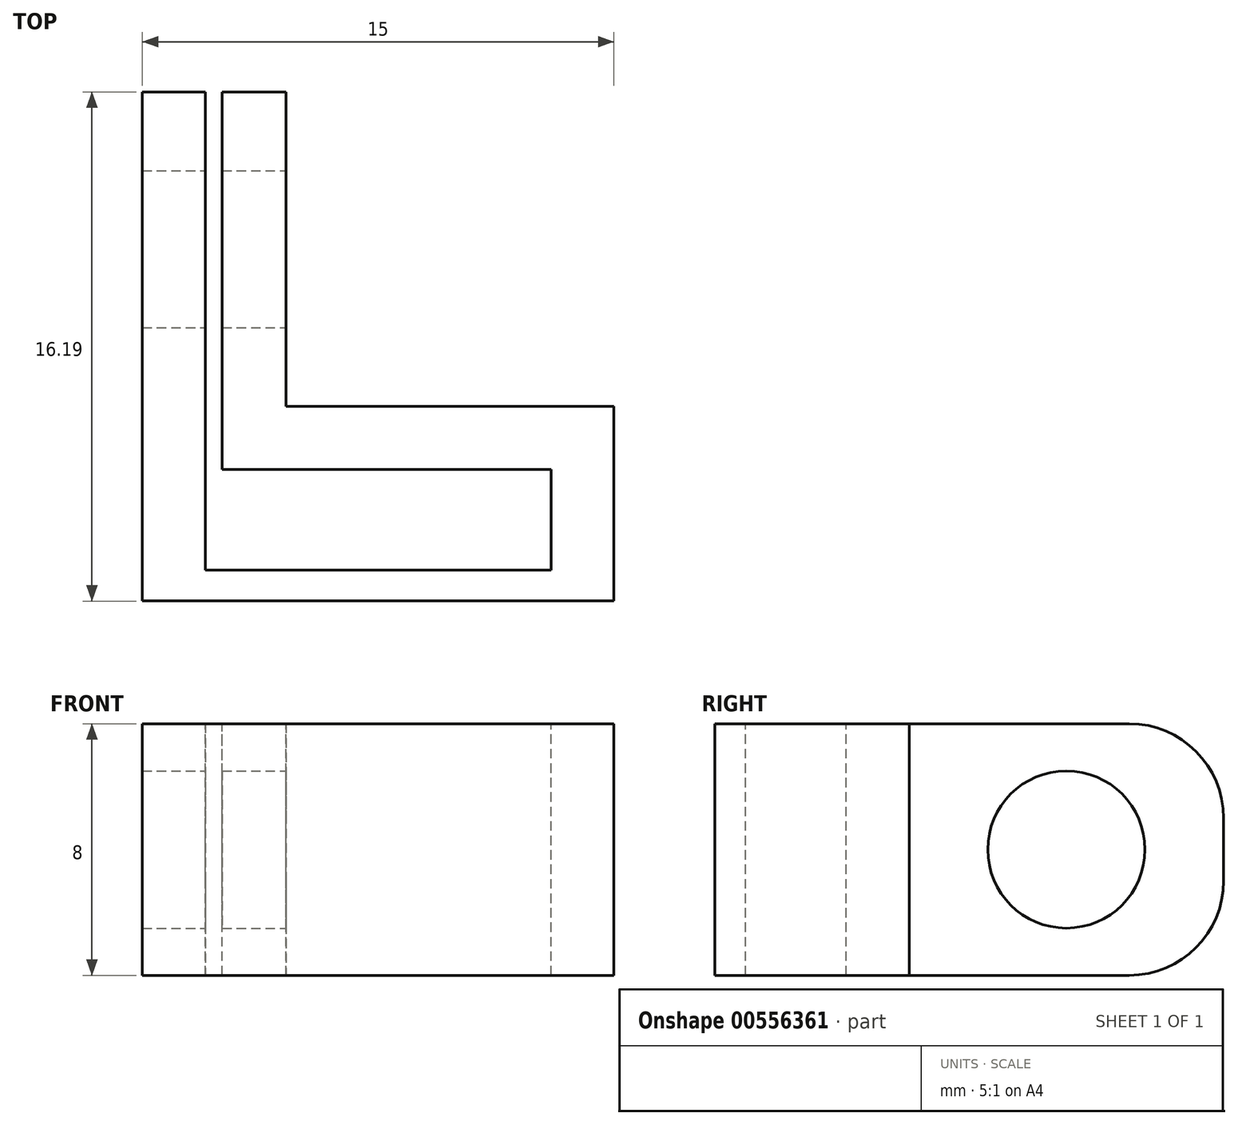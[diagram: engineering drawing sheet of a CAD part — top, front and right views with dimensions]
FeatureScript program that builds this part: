
annotation { "Feature Type Name" : "Feature", "Feature Type Description" : "" }
export const myFeature = defineFeature(function(context is Context, id is Id, definition is map)
    precondition{}
    {
        {
            var Q0;
            Q0=qCreatedBy(makeId("Top.planeOp"),FACE);
            var sketch = newSketch(context, id + "F0", { "sketchPlane" : qUnion([Q0])});
            skLineSegment(sketch, "E0", {"start": v(0, 15.2) * mm, "end": v(0, 0) * mm});
            skLineSegment(sketch, "E1", {"start": v(0, 0) * mm, "end": v(11, 0) * mm});
            skLineSegment(sketch, "E2", {"start": v(11, 0) * mm, "end": v(11, 3.2) * mm});
            skLineSegment(sketch, "E3", {"start": v(11, 3.2) * mm, "end": v(0.54, 3.2) * mm});
            skLineSegment(sketch, "E4", {"start": v(0.54, 3.2) * mm, "end": v(0.54, 15.2) * mm});
            skLineSegment(sketch, "E5", {"start": v(0.54, 15.2) * mm, "end": v(0.57, 15.2) * mm});
            skLineSegment(sketch, "E6", {"start": v(2.57, 5.2) * mm, "end": v(13, 5.2) * mm});
            skLineSegment(sketch, "E7", {"start": v(13, 5.2) * mm, "end": v(13, -0.99) * mm});
            skLineSegment(sketch, "E8", {"start": v(13, -0.99) * mm, "end": v(-2, -0.99) * mm});
            skLineSegment(sketch, "E9", {"start": v(-2, -0.99) * mm, "end": v(-2, 15.2) * mm});
            skLineSegment(sketch, "E10", {"start": v(-2, 15.2) * mm, "end": v(0, 15.2) * mm});
            skLineSegment(sketch, "E11", {"start": v(0.57, 15.2) * mm, "end": v(2.57, 15.2) * mm});
            skLineSegment(sketch, "E12", {"start": v(2.57, 15.2) * mm, "end": v(2.57, 5.2) * mm});
            skSolve(sketch);
        }
        {
            var Q0;
            Q0 = qSketchRegion(id + "F0", true);
            extrude(context, id + "F1", {"entities" : qUnion([Q0]), "oppositeDirection" : true, "depth" : 8 * mm, "offsetDistance" : 25 * mm});
        }
        {
            var Q0;
            Q0=makeQuery(id+"F1.opExtrude","SWEPT_FACE",FACE,{"disambiguationData":[OSD([sQuery(id+"F0.wireOp",EDGE,"E12")])]});
            var sketch = newSketch(context, id + "F2", { "sketchPlane" : qUnion([Q0])});
            skCircle(sketch, "E13", {"center": v(10.2, -4) * mm, "radius": 2.5 * mm});
            skSolve(sketch);
        }
        {
            var Q0;
            Q0=makeQuery(id+"F1.opExtrude","CAP_EDGE",EDGE,{"disambiguationData":[OSD([sQuery(id+"F0.wireOp",EDGE,"E5"),sQuery(id+"F0.wireOp",EDGE,"E11")])],"isStart":true});
            var Q1;
            Q1=makeQuery(id+"F1.opExtrude","CAP_EDGE",EDGE,{"disambiguationData":[OSD([sQuery(id+"F0.wireOp",EDGE,"E10")])],"isStart":true});
            var Q2;
            Q2=makeQuery(id+"F1.opExtrude","CAP_EDGE",EDGE,{"disambiguationData":[OSD([sQuery(id+"F0.wireOp",EDGE,"E10")])],"isStart":false});
            var Q3;
            Q3=makeQuery(id+"F1.opExtrude","CAP_EDGE",EDGE,{"disambiguationData":[OSD([sQuery(id+"F0.wireOp",EDGE,"E5"),sQuery(id+"F0.wireOp",EDGE,"E11")])],"isStart":false});
            fillet(context, id + "F3", {"entities" : qUnion([Q0, Q1, Q2, Q3]), "radius" : 3 * mm, "tangentPropagation" : true, "allowEdgeOverflow" : false});
        }
        {
            var Q0;
            Q0=makeQuery(id+"F2.imprint","IMPRINT",FACE,{"disambiguationData":[TD([[makeQuery(id+"F2.imprint","IMPRINT",EDGE,{"derivedFrom":sQuery(id+"F2.wireOp",EDGE,"E13")}),1.0]])]});
            extrude(context, id + "F4", {"entities" : qUnion([Q0]), "operationType" : NewBodyOperationType.REMOVE, "endBound" : BoundingType.THROUGH_ALL, "oppositeDirection" : true, "depth" : 25 * mm, "offsetDistance" : 25 * mm});
        }
    });
